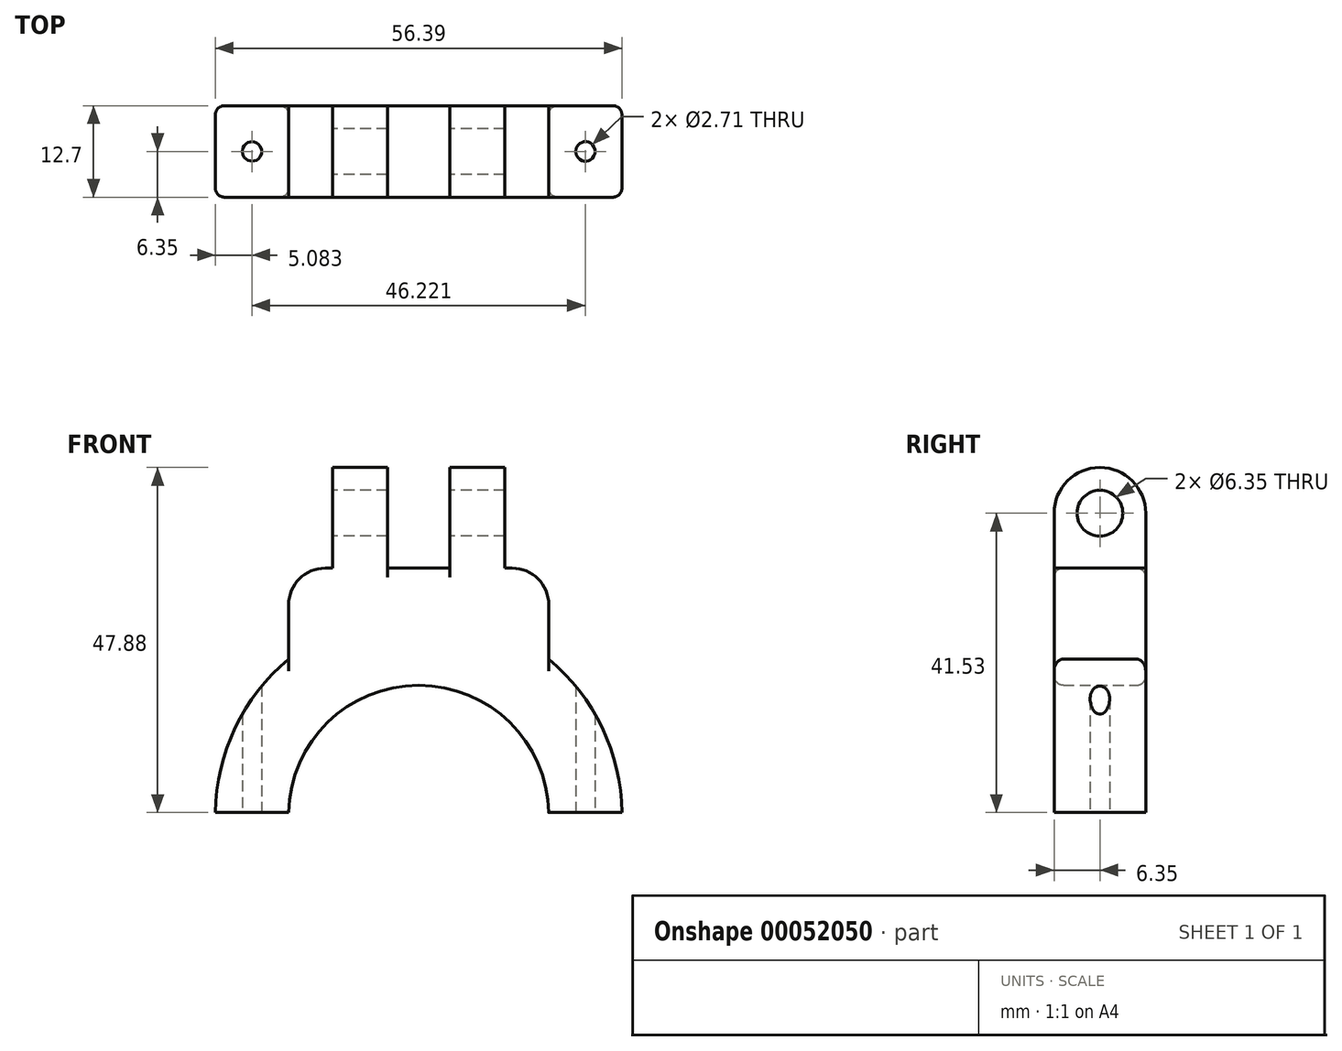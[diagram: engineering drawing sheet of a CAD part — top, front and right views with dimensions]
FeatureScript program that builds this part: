
annotation { "Feature Type Name" : "Feature", "Feature Type Description" : "" }
export const myFeature = defineFeature(function(context is Context, id is Id, definition is map)
    precondition{}
    {
        {
            var Q0;
            Q0=qCreatedBy(makeId("Front.planeOp"),FACE);
            var sketch = newSketch(context, id + "F0", { "sketchPlane" : qUnion([Q0])});
            skLineSegment(sketch, "E0", {"start": v(0, 0) * mm, "end": v(10.16, 0) * mm});
            skLineSegment(sketch, "E1", {"start": v(0, 0) * mm, "end": v(56.39, 0) * mm});
            skLineSegment(sketch, "E2", {"start": v(56.39, 0) * mm, "end": v(46.23, 0) * mm});
            skArc(sketch, "E3", {"start": v(46.23, 0) * mm, "mid": v(28.2, 18.03) * mm, "end": v(10.16, 0) * mm});
            skArc(sketch, "E4", {"start": v(56.39, 0) * mm, "mid": v(28.2, 28.2) * mm, "end": v(0, 0) * mm});
            skLineSegment(sketch, "E5", {"start": v(56.39, 0) * mm, "end": v(56.39, 0.38) * mm});
            skLineSegment(sketch, "E6", {"start": v(0, 0) * mm, "end": v(0, 0.38) * mm});
            skLineSegment(sketch, "E7", {"start": v(56.39, 0.38) * mm, "end": v(46.22, 0.38) * mm});
            skLineSegment(sketch, "E8", {"start": v(0, 0.38) * mm, "end": v(10.16, 0.38) * mm});
            skSolve(sketch);
        }
        {
            var Q0;
            {var subQ0=sQuery(id+"F0.wireOp",EDGE,"E7");var subQ1=sQuery(id+"F0.wireOp",EDGE,"E3");var subQ2=makeQuery(id+"F0.imprint","INTERSECT",VERTEX,{"derivedFrom":[subQ1,subQ0]});Q0=makeQuery(id+"F0.imprint","IMPRINT",FACE,{"disambiguationData":[TD([[makeQuery(id+"F0.imprint","IMPRINT",EDGE,{"disambiguationData":[TD([[subQ2,-1.0]])],"derivedFrom":subQ1}),-1.0]])]});}
            extrude(context, id + "F1", {"entities" : qUnion([Q0]), "depth" : 12.7 * mm});
        }
        {
            var Q0;
            Q0=qCreatedBy(makeId("Top.planeOp"),FACE);
            cPlane(context, id + "F2", {"entities" : qUnion([Q0]), "cplaneType" : CPlaneType.OFFSET, "offset" : 34.3 * mm, "width" : 152.4 * mm, "height" : 152.4 * mm});
        }
        {
            var Q0;
            Q0=qCreatedBy(id+"F2.planeOp",FACE);
            var sketch = newSketch(context, id + "F3", { "sketchPlane" : qUnion([Q0])});
            skLineSegment(sketch, "E9", {"start": v(0, 0) * mm, "end": v(28.2, 0) * mm});
            skLineSegment(sketch, "E10", {"start": v(28.2, 0) * mm, "end": v(10.16, 0) * mm});
            skLineSegment(sketch, "E11", {"start": v(28.2, 0) * mm, "end": v(46.23, 0) * mm});
            skLineSegment(sketch, "E12", {"start": v(10.16, 0) * mm, "end": v(10.16, -12.7) * mm});
            skLineSegment(sketch, "E13", {"start": v(46.23, 0) * mm, "end": v(46.23, -12.7) * mm});
            skLineSegment(sketch, "E14", {"start": v(10.16, -12.7) * mm, "end": v(46.23, -12.7) * mm});
            skSolve(sketch);
        }
        {
            var Q0;
            Q0 = qSketchRegion(id + "F3", true);
            var Q1;
            Q1=makeQuery(id+"F1.opExtrude","SWEPT_FACE",FACE,{"disambiguationData":[OSD([sQuery(id+"F0.wireOp",EDGE,"E4")])]});
            extrude(context, id + "F4", {"entities" : qUnion([Q0]), "operationType" : NewBodyOperationType.ADD, "endBound" : BoundingType.UP_TO_SURFACE, "oppositeDirection" : true, "endBoundEntityFace" : qUnion([Q1]), "depth" : 25.4 * mm});
        }
        {
            var Q0;
            Q0=makeQuery(id+"F4.opExtrude","CAP_FACE",FACE,{"disambiguationData":[OSD([sQuery(id+"F3.wireOp",EDGE,"E10"),sQuery(id+"F3.wireOp",EDGE,"E11"),sQuery(id+"F3.wireOp",EDGE,"E12"),sQuery(id+"F3.wireOp",EDGE,"E13"),sQuery(id+"F3.wireOp",EDGE,"E14")])],"isStart":true});
            var sketch = newSketch(context, id + "F5", { "sketchPlane" : qUnion([Q0])});
            skLineSegment(sketch, "E15", {"start": v(28.2, 0) * mm, "end": v(23.88, 0) * mm});
            skLineSegment(sketch, "E16", {"start": v(28.2, 0) * mm, "end": v(32.51, 0) * mm});
            skLineSegment(sketch, "E17", {"start": v(23.88, 0) * mm, "end": v(16.26, 0) * mm});
            skLineSegment(sketch, "E18", {"start": v(32.51, 0) * mm, "end": v(40.13, 0) * mm});
            skLineSegment(sketch, "E19", {"start": v(16.26, 0) * mm, "end": v(16.26, -12.7) * mm});
            skLineSegment(sketch, "E20", {"start": v(23.88, 0) * mm, "end": v(23.88, -12.7) * mm});
            skLineSegment(sketch, "E21", {"start": v(32.51, 0) * mm, "end": v(32.51, -12.7) * mm});
            skLineSegment(sketch, "E22", {"start": v(40.13, 0) * mm, "end": v(40.13, -12.7) * mm});
            skLineSegment(sketch, "E23", {"start": v(16.26, -12.7) * mm, "end": v(23.88, -12.7) * mm});
            skLineSegment(sketch, "E24", {"start": v(32.51, -12.7) * mm, "end": v(40.13, -12.7) * mm});
            skSolve(sketch);
        }
        {
            var Q0;
            Q0=makeQuery(id+"F5.imprint","IMPRINT",FACE,{"disambiguationData":[TD([[makeQuery(id+"F5.imprint","IMPRINT",EDGE,{"derivedFrom":sQuery(id+"F5.wireOp",EDGE,"E17")}),-1.0]])]});
            var Q1;
            Q1=makeQuery(id+"F5.imprint","IMPRINT",FACE,{"disambiguationData":[TD([[makeQuery(id+"F5.imprint","IMPRINT",EDGE,{"derivedFrom":sQuery(id+"F5.wireOp",EDGE,"E18")}),-1.0]])]});
            extrude(context, id + "F6", {"entities" : qUnion([Q0, Q1]), "operationType" : NewBodyOperationType.ADD, "depth" : 13.97 * mm});
        }
        {
            var Q0;
            Q0=makeQuery(id+"F6.opExtrude","SWEPT_FACE",FACE,{"disambiguationData":[OSD([sQuery(id+"F5.wireOp",EDGE,"E19")])]});
            var sketch = newSketch(context, id + "F7", { "sketchPlane" : qUnion([Q0])});
            skLineSegment(sketch, "E25", {"start": v(6.35, 48.26) * mm, "end": v(6.35, 41.91) * mm});
            skCircle(sketch, "E26", {"center": v(6.35, 41.91) * mm, "radius": 3.18 * mm});
            skSolve(sketch);
        }
        {
            var Q0;
            Q0=makeQuery(id+"F7.imprint","IMPRINT",FACE,{"disambiguationData":[TD([[makeQuery(id+"F7.imprint","IMPRINT",EDGE,{"derivedFrom":sQuery(id+"F7.wireOp",EDGE,"E26")}),1.0]])]});
            var Q1;
            Q1=makeQuery(id+"F6.opExtrude","SWEPT_FACE",FACE,{"disambiguationData":[OSD([sQuery(id+"F5.wireOp",EDGE,"E22")])]});
            extrude(context, id + "F8", {"entities" : qUnion([Q0]), "operationType" : NewBodyOperationType.REMOVE, "endBound" : BoundingType.UP_TO_SURFACE, "oppositeDirection" : true, "endBoundEntityFace" : qUnion([Q1]), "depth" : 25.4 * mm});
        }
        {
            var Q0;
            Q0=makeQuery(id+"F6.opExtrude","CAP_EDGE",EDGE,{"disambiguationData":[OSD([sQuery(id+"F5.wireOp",EDGE,"E23")])],"isStart":false});
            var Q1;
            Q1=makeQuery(id+"F6.opExtrude","CAP_EDGE",EDGE,{"disambiguationData":[OSD([sQuery(id+"F5.wireOp",EDGE,"E17")])],"isStart":false});
            var Q2;
            Q2=makeQuery(id+"F6.opExtrude","CAP_EDGE",EDGE,{"disambiguationData":[OSD([sQuery(id+"F5.wireOp",EDGE,"E24")])],"isStart":false});
            var Q3;
            Q3=makeQuery(id+"F6.opExtrude","CAP_EDGE",EDGE,{"disambiguationData":[OSD([sQuery(id+"F5.wireOp",EDGE,"E18")])],"isStart":false});
            fillet(context, id + "F9", {"entities" : qUnion([Q0, Q1, Q2, Q3]), "radius" : 6.35 * mm, "tangentPropagation" : true, "allowEdgeOverflow" : false});
        }
        {
            var Q0;
            Q0=makeQuery(id+"F4.opExtrude","CAP_EDGE",EDGE,{"disambiguationData":[OSD([sQuery(id+"F3.wireOp",EDGE,"E12")])],"isStart":true});
            var Q1;
            Q1=makeQuery(id+"F4.opExtrude","TWEAK_EDGE",EDGE,{"derivedFrom":[makeQuery(id+"F1.opExtrude","SWEPT_FACE",FACE,{"disambiguationData":[OSD([sQuery(id+"F0.wireOp",EDGE,"E4")])]}),makeQuery(id+"F3.imprint","IMPRINT",EDGE,{"derivedFrom":sQuery(id+"F3.wireOp",EDGE,"E12")})]});
            var Q2;
            Q2=makeQuery(id+"F4.opExtrude","CAP_EDGE",EDGE,{"disambiguationData":[OSD([sQuery(id+"F3.wireOp",EDGE,"E13")])],"isStart":true});
            var Q3;
            Q3=makeQuery(id+"F4.opExtrude","TWEAK_EDGE",EDGE,{"derivedFrom":[makeQuery(id+"F1.opExtrude","SWEPT_FACE",FACE,{"disambiguationData":[OSD([sQuery(id+"F0.wireOp",EDGE,"E4")])]}),makeQuery(id+"F3.imprint","IMPRINT",EDGE,{"derivedFrom":sQuery(id+"F3.wireOp",EDGE,"E13")})]});
            fillet(context, id + "F10", {"entities" : qUnion([Q0, Q1, Q2, Q3]), "radius" : 5.08 * mm, "tangentPropagation" : true, "allowEdgeOverflow" : false});
        }
        {
            var Q0;
            Q0=makeQuery(id+"F1.opExtrude","SWEPT_FACE",FACE,{"disambiguationData":[OSD([sQuery(id+"F0.wireOp",EDGE,"E7")])]});
            var sketch = newSketch(context, id + "F11", { "sketchPlane" : qUnion([Q0])});
            skLineSegment(sketch, "E27", {"start": v(51.3, 12.7) * mm, "end": v(51.3, 6.35) * mm});
            skCircle(sketch, "E28", {"center": v(51.3, 6.35) * mm, "radius": 1.35 * mm});
            skSolve(sketch);
        }
        {
            var Q0;
            Q0=makeQuery(id+"F11.imprint","IMPRINT",FACE,{"disambiguationData":[TD([[makeQuery(id+"F11.imprint","IMPRINT",EDGE,{"derivedFrom":sQuery(id+"F11.wireOp",EDGE,"E28")}),1.0]])]});
            var Q1;
            {var subQ1=sQuery(id+"F0.wireOp",EDGE,"E7");var subQ2=sQuery(id+"F0.wireOp",EDGE,"E4");Q1=makeQuery(id+"F4.boolean.opBoolean","SPLIT",FACE,{"disambiguationData":[TD([makeQuery(id+"F1.opExtrude","SWEPT_FACE",FACE,{"disambiguationData":[OSD([subQ1])]})])],"derivedFrom":makeQuery(id+"F1.opExtrude","SWEPT_FACE",FACE,{"disambiguationData":[OSD([subQ2])]})});}
            extrude(context, id + "F12", {"entities" : qUnion([Q0]), "operationType" : NewBodyOperationType.REMOVE, "endBound" : BoundingType.UP_TO_SURFACE, "oppositeDirection" : true, "endBoundEntityFace" : qUnion([Q1]), "depth" : 25.4 * mm});
        }
        {
            var Q0;
            Q0=makeQuery(id+"F1.opExtrude","SWEPT_FACE",FACE,{"disambiguationData":[OSD([sQuery(id+"F0.wireOp",EDGE,"E8")])]});
            var sketch = newSketch(context, id + "F13", { "sketchPlane" : qUnion([Q0])});
            skLineSegment(sketch, "E29", {"start": v(5.08, 12.7) * mm, "end": v(5.08, 6.35) * mm});
            skPoint(sketch, "E29.endSnap0", {"position": v(5.08, 12.7) * mm});
            skCircle(sketch, "E30", {"center": v(5.08, 6.35) * mm, "radius": 1.35 * mm});
            skSolve(sketch);
        }
        {
            var Q0;
            Q0=makeQuery(id+"F13.imprint","IMPRINT",FACE,{"disambiguationData":[TD([[makeQuery(id+"F13.imprint","IMPRINT",EDGE,{"derivedFrom":sQuery(id+"F13.wireOp",EDGE,"E30")}),1.0]])]});
            var Q1;
            {var subQ0=sQuery(id+"F0.wireOp",EDGE,"E8");var subQ2=sQuery(id+"F0.wireOp",EDGE,"E4");Q1=makeQuery(id+"F4.boolean.opBoolean","SPLIT",FACE,{"disambiguationData":[TD([makeQuery(id+"F1.opExtrude","SWEPT_FACE",FACE,{"disambiguationData":[OSD([subQ0])]})])],"derivedFrom":makeQuery(id+"F1.opExtrude","SWEPT_FACE",FACE,{"disambiguationData":[OSD([subQ2])]})});}
            extrude(context, id + "F14", {"entities" : qUnion([Q0]), "operationType" : NewBodyOperationType.REMOVE, "endBound" : BoundingType.UP_TO_SURFACE, "oppositeDirection" : true, "endBoundEntityFace" : qUnion([Q1]), "depth" : 25.4 * mm});
        }
        {
            var Q0;
            Q0=makeQuery(id+"F1.opExtrude","CAP_EDGE",EDGE,{"disambiguationData":[OSD([sQuery(id+"F0.wireOp",EDGE,"E3")])],"isStart":true});
            var Q1;
            {var subQ0=sQuery(id+"F0.wireOp",EDGE,"E8");var subQ1=sQuery(id+"F0.wireOp",EDGE,"E4");Q1=makeQuery(id+"F4.boolean.opBoolean","SPLIT",EDGE,{"disambiguationData":[TD([makeQuery(id+"F1.opExtrude","SWEPT_FACE",FACE,{"disambiguationData":[OSD([subQ0])]})])],"derivedFrom":makeQuery(id+"F1.opExtrude","CAP_EDGE",EDGE,{"disambiguationData":[OSD([subQ1])],"isStart":true})});}
            var Q2;
            {var subQ0=sQuery(id+"F0.wireOp",EDGE,"E8");var subQ1=sQuery(id+"F0.wireOp",EDGE,"E4");Q2=makeQuery(id+"F4.boolean.opBoolean","SPLIT",EDGE,{"disambiguationData":[TD([makeQuery(id+"F1.opExtrude","SWEPT_FACE",FACE,{"disambiguationData":[OSD([subQ0])]})])],"derivedFrom":makeQuery(id+"F1.opExtrude","CAP_EDGE",EDGE,{"disambiguationData":[OSD([subQ1])],"isStart":false})});}
            var Q3;
            Q3=makeQuery(id+"F1.opExtrude","CAP_EDGE",EDGE,{"disambiguationData":[OSD([sQuery(id+"F0.wireOp",EDGE,"E3")])],"isStart":false});
            var Q4;
            {var subQ0=sQuery(id+"F0.wireOp",EDGE,"E7");var subQ1=sQuery(id+"F0.wireOp",EDGE,"E4");Q4=makeQuery(id+"F4.boolean.opBoolean","SPLIT",EDGE,{"disambiguationData":[TD([makeQuery(id+"F1.opExtrude","SWEPT_FACE",FACE,{"disambiguationData":[OSD([subQ0])]})])],"derivedFrom":makeQuery(id+"F1.opExtrude","CAP_EDGE",EDGE,{"disambiguationData":[OSD([subQ1])],"isStart":false})});}
            var Q5;
            {var subQ0=sQuery(id+"F0.wireOp",EDGE,"E7");var subQ1=sQuery(id+"F0.wireOp",EDGE,"E4");Q5=makeQuery(id+"F4.boolean.opBoolean","SPLIT",EDGE,{"disambiguationData":[TD([makeQuery(id+"F1.opExtrude","SWEPT_FACE",FACE,{"disambiguationData":[OSD([subQ0])]})])],"derivedFrom":makeQuery(id+"F1.opExtrude","CAP_EDGE",EDGE,{"disambiguationData":[OSD([subQ1])],"isStart":true})});}
            var Q6;
            {var subQ0=sQuery(id+"F3.wireOp",EDGE,"E11");var subQ1=sQuery(id+"F3.wireOp",EDGE,"E10");Q6=makeQuery(id+"F6.boolean.opBoolean","SPLIT",EDGE,{"disambiguationData":[TD([makeQuery(id+"F6.opExtrude","SWEPT_FACE",FACE,{"disambiguationData":[OSD([sQuery(id+"F5.wireOp",EDGE,"E20")])]})])],"derivedFrom":makeQuery(id+"F4.opExtrude","CAP_EDGE",EDGE,{"disambiguationData":[OSD([subQ1,subQ0])],"isStart":true})});}
            var Q7;
            {var subQ0=sQuery(id+"F3.wireOp",EDGE,"E14");Q7=makeQuery(id+"F6.boolean.opBoolean","SPLIT",EDGE,{"disambiguationData":[TD([makeQuery(id+"F6.opExtrude","SWEPT_FACE",FACE,{"disambiguationData":[OSD([sQuery(id+"F5.wireOp",EDGE,"E20")])]})])],"derivedFrom":makeQuery(id+"F4.opExtrude","CAP_EDGE",EDGE,{"disambiguationData":[OSD([subQ0])],"isStart":true})});}
            fillet(context, id + "F15", {"entities" : qUnion([Q0, Q1, Q2, Q3, Q4, Q5, Q6, Q7]), "radius" : 1.27 * mm, "tangentPropagation" : true, "allowEdgeOverflow" : false});
        }
    });
